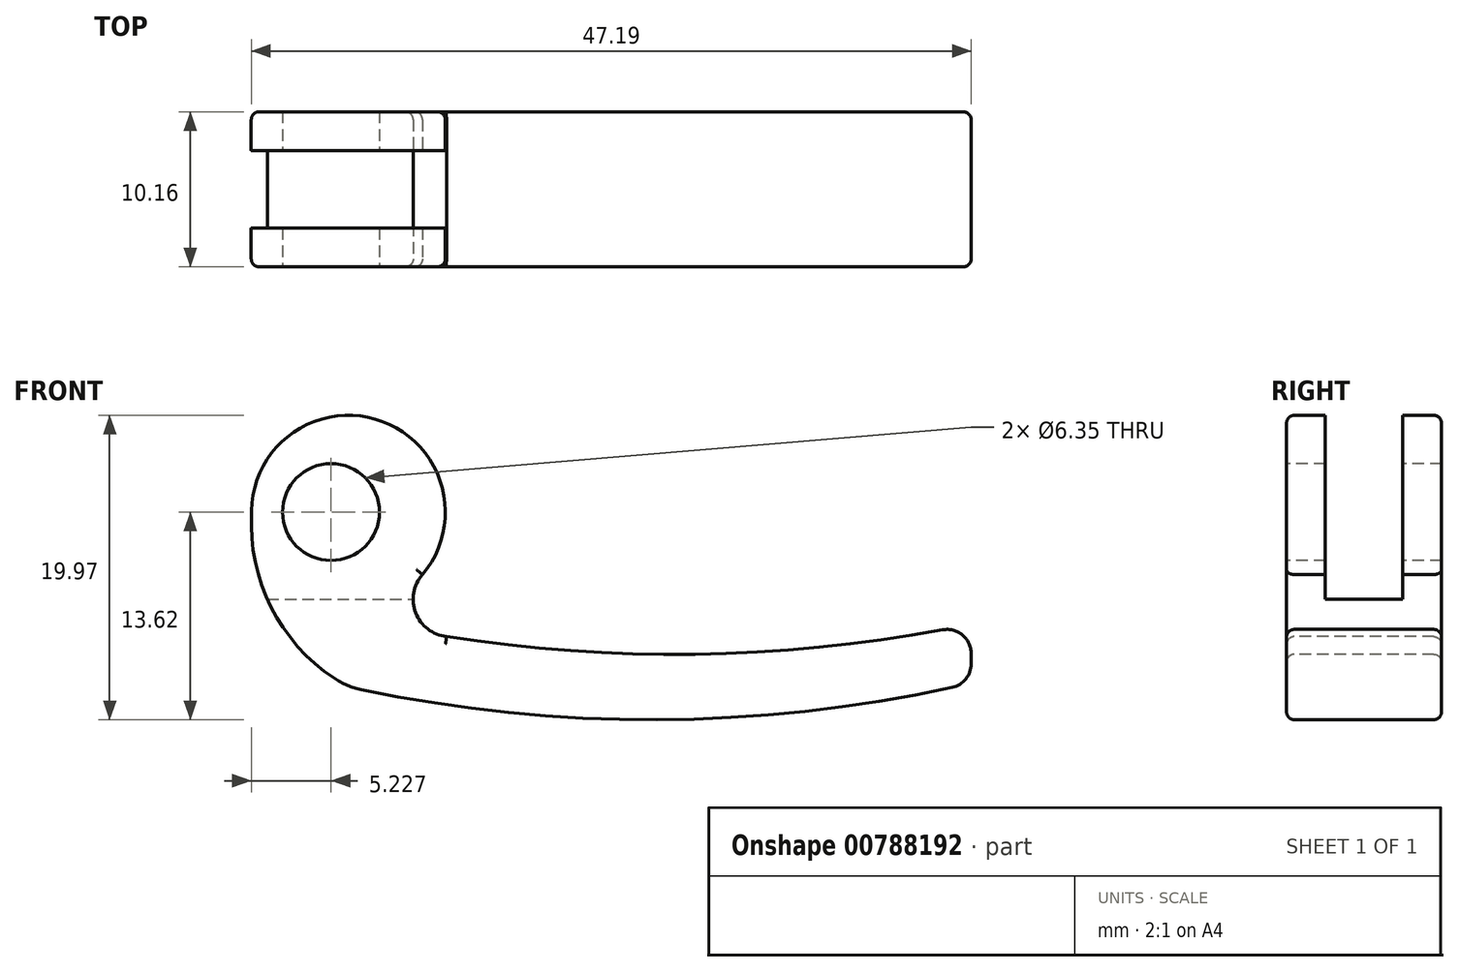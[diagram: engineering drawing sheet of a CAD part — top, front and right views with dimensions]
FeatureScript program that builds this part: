
annotation { "Feature Type Name" : "Feature", "Feature Type Description" : "" }
export const myFeature = defineFeature(function(context is Context, id is Id, definition is map)
    precondition{}
    {
        {
            var Q0;
            Q0=qCreatedBy(makeId("Front.planeOp"),FACE);
            var sketch = newSketch(context, id + "F0", { "sketchPlane" : qUnion([Q0])});
            skArc(sketch, "E0", {"start": v(4.85, -4.1) * mm, "mid": v(2.18, 5.96) * mm, "end": v(-6.35, 0) * mm});
            skCircle(sketch, "E1", {"center": v(-1.14, 0) * mm, "radius": 3.18 * mm});
            skArc(sketch, "E2", {"start": v(4.85, -4.1) * mm, "mid": v(4.41, -6.61) * mm, "end": v(6.43, -8.17) * mm});
            skLineSegment(sketch, "E3", {"start": v(40.82, -11.22) * mm, "end": v(40.82, -7.36) * mm});
            skArc(sketch, "E4", {"start": v(-6.35, 0) * mm, "mid": v(-4.84, -6.66) * mm, "end": v(0, -11.47) * mm});
            skPoint(sketch, "E5.end.orphan", {"position": v(-7.62, -12.7) * mm});
            skArc(sketch, "E6", {"start": v(6.43, -8.17) * mm, "mid": v(23.66, -9.3) * mm, "end": v(40.82, -7.36) * mm});
            skArc(sketch, "E7", {"start": v(0, -11.47) * mm, "mid": v(20.43, -13.62) * mm, "end": v(40.82, -11.22) * mm});
            skSolve(sketch);
        }
        {
            var Q0;
            Q0=qSketchRegion(id+"F0",true);
            extrude(context, id + "F1", {"entities" : qUnion([Q0]), "oppositeDirection" : true, "depth" : 10.16 * mm});
        }
        {
            var Q0;
            Q0=makeQuery(id+"F1.opExtrude","SWEPT_EDGE",EDGE,{"disambiguationData":[OSD([sQuery(id+"F0.wireOp",EDGE,"E3"),sQuery(id+"F0.wireOp",EDGE,"0e92d39d-9146-4402-9eeb-864c5b0dd509.trimOffspring")])]});
            var Q1;
            Q1=makeQuery(id+"F1.opExtrude","SWEPT_EDGE",EDGE,{"disambiguationData":[OSD([sQuery(id+"F0.wireOp",EDGE,"416955f1-9108-4c35-9a88-784f55616ef5"),sQuery(id+"F0.wireOp",EDGE,"E3")])]});
            fillet(context, id + "F2", {"entities" : qUnion([Q0, Q1]), "radius" : 1.57 * mm, "tangentPropagation" : true, "allowEdgeOverflow" : false});
        }
        {
            var Q0;
            Q0=makeQuery(id+"F1.opExtrude","SWEPT_EDGE",EDGE,{"disambiguationData":[OSD([sQuery(id+"F0.wireOp",EDGE,"416955f1-9108-4c35-9a88-784f55616ef5"),sQuery(id+"F0.wireOp",EDGE,"E4")])]});
            fillet(context, id + "F3", {"entities" : qUnion([Q0]), "radius" : 5.08 * mm, "tangentPropagation" : true, "allowEdgeOverflow" : false});
        }
        {
            var Q0;
            Q0=qCreatedBy(makeId("Right.planeOp"),FACE);
            var sketch = newSketch(context, id + "F4", { "sketchPlane" : qUnion([Q0])});
            skLineSegment(sketch, "E8.bottom", {"start": v(2.54, 7.62) * mm, "end": v(7.62, 7.62) * mm});
            skLineSegment(sketch, "E8.top", {"start": v(2.54, -5.72) * mm, "end": v(7.62, -5.72) * mm});
            skLineSegment(sketch, "E8.left", {"start": v(2.54, 7.62) * mm, "end": v(2.54, -5.72) * mm});
            skLineSegment(sketch, "E8.right", {"start": v(7.62, 7.62) * mm, "end": v(7.62, -5.72) * mm});
            skSolve(sketch);
        }
        {
            var Q0;
            Q0=qSketchRegion(id+"F4",true);
            extrude(context, id + "F5", {"entities" : qUnion([Q0]), "operationType" : NewBodyOperationType.REMOVE, "endBound" : BoundingType.SYMMETRIC, "oppositeDirection" : true, "depth" : 25.4 * mm});
        }
        {
            var Q0;
            Q0=makeQuery(id+"F1.opExtrude","CAP_EDGE",EDGE,{"disambiguationData":[OSD([sQuery(id+"F0.wireOp",EDGE,"E0")])],"isStart":true});
            var Q1;
            Q1=makeQuery(id+"F1.opExtrude","CAP_EDGE",EDGE,{"disambiguationData":[OSD([sQuery(id+"F0.wireOp",EDGE,"E4")])],"isStart":true});
            var Q2;
            {var subQ0=sQuery(id+"F0.wireOp",EDGE,"E4");var subQ1=sQuery(id+"F0.wireOp",EDGE,"416955f1-9108-4c35-9a88-784f55616ef5");Q2=makeQuery(id+"F3.opFillet","BLEND_EDGE",EDGE,{"blendedFrom":[makeQuery(id+"F1.opExtrude","SWEPT_EDGE",EDGE,{"disambiguationData":[OSD([subQ1,subQ0])]}),makeQuery(id+"F1.opExtrude","CAP_FACE",FACE,{"disambiguationData":[OSD([sQuery(id+"F0.wireOp",EDGE,"E0"),sQuery(id+"F0.wireOp",EDGE,"E1"),subQ1,sQuery(id+"F0.wireOp",EDGE,"E2"),sQuery(id+"F0.wireOp",EDGE,"E3"),subQ0,sQuery(id+"F0.wireOp",EDGE,"0e92d39d-9146-4402-9eeb-864c5b0dd509.trimOffspring")])],"isStart":true})],"blendedInto":[makeQuery(id+"F1.opExtrude","CAP_FACE",FACE,{"disambiguationData":[OSD([sQuery(id+"F0.wireOp",EDGE,"E0"),sQuery(id+"F0.wireOp",EDGE,"E1"),subQ1,sQuery(id+"F0.wireOp",EDGE,"E2"),sQuery(id+"F0.wireOp",EDGE,"E3"),subQ0,sQuery(id+"F0.wireOp",EDGE,"0e92d39d-9146-4402-9eeb-864c5b0dd509.trimOffspring")])],"isStart":true})]});}
            var Q3;
            Q3=makeQuery(id+"F1.opExtrude","CAP_EDGE",EDGE,{"disambiguationData":[OSD([sQuery(id+"F0.wireOp",EDGE,"416955f1-9108-4c35-9a88-784f55616ef5")])],"isStart":true});
            var Q4;
            Q4=makeQuery(id+"F1.opExtrude","CAP_EDGE",EDGE,{"disambiguationData":[OSD([sQuery(id+"F0.wireOp",EDGE,"E2")])],"isStart":true});
            var Q5;
            Q5=makeQuery(id+"F1.opExtrude","CAP_EDGE",EDGE,{"disambiguationData":[OSD([sQuery(id+"F0.wireOp",EDGE,"0e92d39d-9146-4402-9eeb-864c5b0dd509.trimOffspring")])],"isStart":true});
            var Q6;
            {var subQ0=sQuery(id+"F0.wireOp",EDGE,"0e92d39d-9146-4402-9eeb-864c5b0dd509.trimOffspring");var subQ1=sQuery(id+"F0.wireOp",EDGE,"E3");Q6=makeQuery(id+"F2.opFillet","BLEND_EDGE",EDGE,{"blendedFrom":[makeQuery(id+"F1.opExtrude","SWEPT_EDGE",EDGE,{"disambiguationData":[OSD([subQ1,subQ0])]}),makeQuery(id+"F1.opExtrude","CAP_FACE",FACE,{"disambiguationData":[OSD([sQuery(id+"F0.wireOp",EDGE,"E0"),sQuery(id+"F0.wireOp",EDGE,"E1"),sQuery(id+"F0.wireOp",EDGE,"416955f1-9108-4c35-9a88-784f55616ef5"),sQuery(id+"F0.wireOp",EDGE,"E2"),subQ1,sQuery(id+"F0.wireOp",EDGE,"E4"),subQ0])],"isStart":true})],"blendedInto":[makeQuery(id+"F1.opExtrude","CAP_FACE",FACE,{"disambiguationData":[OSD([sQuery(id+"F0.wireOp",EDGE,"E0"),sQuery(id+"F0.wireOp",EDGE,"E1"),sQuery(id+"F0.wireOp",EDGE,"416955f1-9108-4c35-9a88-784f55616ef5"),sQuery(id+"F0.wireOp",EDGE,"E2"),subQ1,sQuery(id+"F0.wireOp",EDGE,"E4"),subQ0])],"isStart":true})]});}
            var Q7;
            {var subQ0=sQuery(id+"F0.wireOp",EDGE,"E3");var subQ1=sQuery(id+"F0.wireOp",EDGE,"416955f1-9108-4c35-9a88-784f55616ef5");Q7=makeQuery(id+"F2.opFillet","BLEND_EDGE",EDGE,{"blendedFrom":[makeQuery(id+"F1.opExtrude","SWEPT_EDGE",EDGE,{"disambiguationData":[OSD([subQ1,subQ0])]}),makeQuery(id+"F1.opExtrude","CAP_FACE",FACE,{"disambiguationData":[OSD([sQuery(id+"F0.wireOp",EDGE,"E0"),sQuery(id+"F0.wireOp",EDGE,"E1"),subQ1,sQuery(id+"F0.wireOp",EDGE,"E2"),subQ0,sQuery(id+"F0.wireOp",EDGE,"E4"),sQuery(id+"F0.wireOp",EDGE,"0e92d39d-9146-4402-9eeb-864c5b0dd509.trimOffspring")])],"isStart":true})],"blendedInto":[makeQuery(id+"F1.opExtrude","CAP_FACE",FACE,{"disambiguationData":[OSD([sQuery(id+"F0.wireOp",EDGE,"E0"),sQuery(id+"F0.wireOp",EDGE,"E1"),subQ1,sQuery(id+"F0.wireOp",EDGE,"E2"),subQ0,sQuery(id+"F0.wireOp",EDGE,"E4"),sQuery(id+"F0.wireOp",EDGE,"0e92d39d-9146-4402-9eeb-864c5b0dd509.trimOffspring")])],"isStart":true})]});}
            var Q8;
            Q8=makeQuery(id+"F1.opExtrude","CAP_EDGE",EDGE,{"disambiguationData":[OSD([sQuery(id+"F0.wireOp",EDGE,"E3")])],"isStart":true});
            var Q9;
            Q9=makeQuery(id+"F1.opExtrude","CAP_EDGE",EDGE,{"disambiguationData":[OSD([sQuery(id+"F0.wireOp",EDGE,"E3")])],"isStart":false});
            var Q10;
            {var subQ0=sQuery(id+"F0.wireOp",EDGE,"0e92d39d-9146-4402-9eeb-864c5b0dd509.trimOffspring");var subQ1=sQuery(id+"F0.wireOp",EDGE,"E3");Q10=makeQuery(id+"F2.opFillet","BLEND_EDGE",EDGE,{"blendedFrom":[makeQuery(id+"F1.opExtrude","SWEPT_EDGE",EDGE,{"disambiguationData":[OSD([subQ1,subQ0])]}),makeQuery(id+"F1.opExtrude","CAP_FACE",FACE,{"disambiguationData":[OSD([sQuery(id+"F0.wireOp",EDGE,"E0"),sQuery(id+"F0.wireOp",EDGE,"E1"),sQuery(id+"F0.wireOp",EDGE,"416955f1-9108-4c35-9a88-784f55616ef5"),sQuery(id+"F0.wireOp",EDGE,"E2"),subQ1,sQuery(id+"F0.wireOp",EDGE,"E4"),subQ0])],"isStart":false})],"blendedInto":[makeQuery(id+"F1.opExtrude","CAP_FACE",FACE,{"disambiguationData":[OSD([sQuery(id+"F0.wireOp",EDGE,"E0"),sQuery(id+"F0.wireOp",EDGE,"E1"),sQuery(id+"F0.wireOp",EDGE,"416955f1-9108-4c35-9a88-784f55616ef5"),sQuery(id+"F0.wireOp",EDGE,"E2"),subQ1,sQuery(id+"F0.wireOp",EDGE,"E4"),subQ0])],"isStart":false})]});}
            var Q11;
            Q11=makeQuery(id+"F1.opExtrude","CAP_EDGE",EDGE,{"disambiguationData":[OSD([sQuery(id+"F0.wireOp",EDGE,"0e92d39d-9146-4402-9eeb-864c5b0dd509.trimOffspring")])],"isStart":false});
            var Q12;
            {var subQ0=sQuery(id+"F0.wireOp",EDGE,"E3");var subQ1=sQuery(id+"F0.wireOp",EDGE,"416955f1-9108-4c35-9a88-784f55616ef5");Q12=makeQuery(id+"F2.opFillet","BLEND_EDGE",EDGE,{"blendedFrom":[makeQuery(id+"F1.opExtrude","SWEPT_EDGE",EDGE,{"disambiguationData":[OSD([subQ1,subQ0])]}),makeQuery(id+"F1.opExtrude","CAP_FACE",FACE,{"disambiguationData":[OSD([sQuery(id+"F0.wireOp",EDGE,"E0"),sQuery(id+"F0.wireOp",EDGE,"E1"),subQ1,sQuery(id+"F0.wireOp",EDGE,"E2"),subQ0,sQuery(id+"F0.wireOp",EDGE,"E4"),sQuery(id+"F0.wireOp",EDGE,"0e92d39d-9146-4402-9eeb-864c5b0dd509.trimOffspring")])],"isStart":false})],"blendedInto":[makeQuery(id+"F1.opExtrude","CAP_FACE",FACE,{"disambiguationData":[OSD([sQuery(id+"F0.wireOp",EDGE,"E0"),sQuery(id+"F0.wireOp",EDGE,"E1"),subQ1,sQuery(id+"F0.wireOp",EDGE,"E2"),subQ0,sQuery(id+"F0.wireOp",EDGE,"E4"),sQuery(id+"F0.wireOp",EDGE,"0e92d39d-9146-4402-9eeb-864c5b0dd509.trimOffspring")])],"isStart":false})]});}
            var Q13;
            Q13=makeQuery(id+"F1.opExtrude","CAP_EDGE",EDGE,{"disambiguationData":[OSD([sQuery(id+"F0.wireOp",EDGE,"416955f1-9108-4c35-9a88-784f55616ef5")])],"isStart":false});
            var Q14;
            {var subQ0=sQuery(id+"F0.wireOp",EDGE,"E4");var subQ1=sQuery(id+"F0.wireOp",EDGE,"416955f1-9108-4c35-9a88-784f55616ef5");Q14=makeQuery(id+"F3.opFillet","BLEND_EDGE",EDGE,{"blendedFrom":[makeQuery(id+"F1.opExtrude","SWEPT_EDGE",EDGE,{"disambiguationData":[OSD([subQ1,subQ0])]}),makeQuery(id+"F1.opExtrude","CAP_FACE",FACE,{"disambiguationData":[OSD([sQuery(id+"F0.wireOp",EDGE,"E0"),sQuery(id+"F0.wireOp",EDGE,"E1"),subQ1,sQuery(id+"F0.wireOp",EDGE,"E2"),sQuery(id+"F0.wireOp",EDGE,"E3"),subQ0,sQuery(id+"F0.wireOp",EDGE,"0e92d39d-9146-4402-9eeb-864c5b0dd509.trimOffspring")])],"isStart":false})],"blendedInto":[makeQuery(id+"F1.opExtrude","CAP_FACE",FACE,{"disambiguationData":[OSD([sQuery(id+"F0.wireOp",EDGE,"E0"),sQuery(id+"F0.wireOp",EDGE,"E1"),subQ1,sQuery(id+"F0.wireOp",EDGE,"E2"),sQuery(id+"F0.wireOp",EDGE,"E3"),subQ0,sQuery(id+"F0.wireOp",EDGE,"0e92d39d-9146-4402-9eeb-864c5b0dd509.trimOffspring")])],"isStart":false})]});}
            var Q15;
            Q15=makeQuery(id+"F1.opExtrude","CAP_EDGE",EDGE,{"disambiguationData":[OSD([sQuery(id+"F0.wireOp",EDGE,"E4")])],"isStart":false});
            var Q16;
            Q16=makeQuery(id+"F1.opExtrude","CAP_EDGE",EDGE,{"disambiguationData":[OSD([sQuery(id+"F0.wireOp",EDGE,"E0")])],"isStart":false});
            var Q17;
            Q17=makeQuery(id+"F1.opExtrude","CAP_EDGE",EDGE,{"disambiguationData":[OSD([sQuery(id+"F0.wireOp",EDGE,"E2")])],"isStart":false});
            fillet(context, id + "F6", {"entities" : qUnion([Q0, Q1, Q2, Q3, Q4, Q5, Q6, Q7, Q8, Q9, Q10, Q11, Q12, Q13, Q14, Q15, Q16, Q17]), "radius" : 0.5 * mm, "tangentPropagation" : true, "allowEdgeOverflow" : false});
        }
    });
